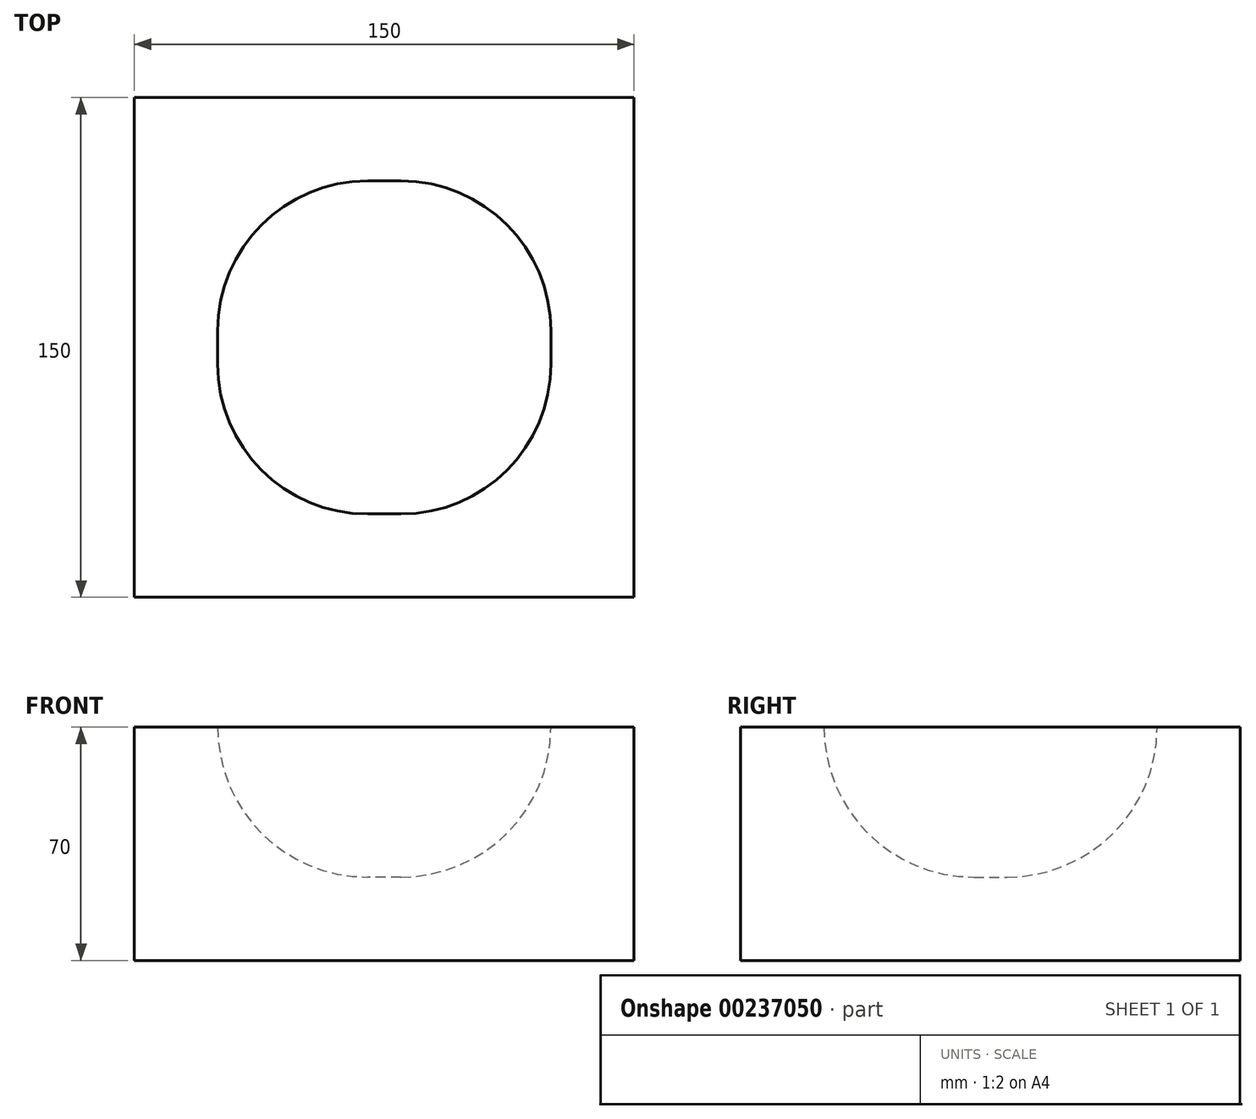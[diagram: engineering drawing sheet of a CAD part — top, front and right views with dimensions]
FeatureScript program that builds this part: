
annotation { "Feature Type Name" : "Feature", "Feature Type Description" : "" }
export const myFeature = defineFeature(function(context is Context, id is Id, definition is map)
    precondition{}
    {
        {
            var Q0;
            Q0=qCreatedBy(makeId("Top.planeOp"),FACE);
            var sketch = newSketch(context, id + "F0", { "sketchPlane" : qUnion([Q0])});
            skLineSegment(sketch, "E0.bottom", {"start": v(75, -75) * mm, "end": v(-75, -75) * mm});
            skLineSegment(sketch, "E0.top", {"start": v(75, 75) * mm, "end": v(-75, 75) * mm});
            skLineSegment(sketch, "E0.left", {"start": v(75, -75) * mm, "end": v(75, 75) * mm});
            skLineSegment(sketch, "E0.right", {"start": v(-75, -75) * mm, "end": v(-75, 75) * mm});
            skPoint(sketch, "E0.middle", {"position": v(0, 0) * mm});
            skSolve(sketch);
        }
        {
            var Q0;
            Q0=makeQuery(id+"F0.imprint","IMPRINT",FACE,{"disambiguationData":[TD([[makeQuery(id+"F0.imprint","IMPRINT",EDGE,{"derivedFrom":sQuery(id+"F0.wireOp",EDGE,"E0.bottom")}),-1.0]])]});
            extrude(context, id + "F1", {"entities" : qUnion([Q0]), "depth" : 70 * mm});
        }
        {
            var Q0;
            Q0=makeQuery(id+"F1.opExtrude","CAP_FACE",FACE,{"disambiguationData":[OSD([sQuery(id+"F0.wireOp",EDGE,"E0.bottom"),sQuery(id+"F0.wireOp",EDGE,"E0.top"),sQuery(id+"F0.wireOp",EDGE,"E0.left"),sQuery(id+"F0.wireOp",EDGE,"E0.right")])],"isStart":false});
            shell(context, id + "F2", {"entities" : qUnion([Q0]), "thickness" : 25 * mm});
        }
        {
            var Q0;
            {var subQ0=sQuery(id+"F0.wireOp",EDGE,"E0.top");Q0=makeQuery(id+"F2.opShell","OFFSET_EDGE",EDGE,{"disambiguationData":[OSD([subQ0]),TDD([makeQuery(id+"F1.opExtrude","CAP_EDGE",EDGE,{"disambiguationData":[OSD([subQ0])],"isStart":true})])]});}
            var Q1;
            {var subQ0=sQuery(id+"F0.wireOp",EDGE,"E0.right");Q1=makeQuery(id+"F2.opShell","OFFSET_EDGE",EDGE,{"disambiguationData":[OSD([subQ0]),TDD([makeQuery(id+"F1.opExtrude","CAP_EDGE",EDGE,{"disambiguationData":[OSD([subQ0])],"isStart":true})])]});}
            var Q2;
            {var subQ0=sQuery(id+"F0.wireOp",EDGE,"E0.left");Q2=makeQuery(id+"F2.opShell","OFFSET_EDGE",EDGE,{"disambiguationData":[OSD([subQ0]),TDD([makeQuery(id+"F1.opExtrude","CAP_EDGE",EDGE,{"disambiguationData":[OSD([subQ0])],"isStart":true})])]});}
            var Q3;
            {var subQ0=sQuery(id+"F0.wireOp",EDGE,"E0.bottom");Q3=makeQuery(id+"F2.opShell","OFFSET_EDGE",EDGE,{"disambiguationData":[OSD([subQ0]),TDD([makeQuery(id+"F1.opExtrude","CAP_EDGE",EDGE,{"disambiguationData":[OSD([subQ0])],"isStart":true})])]});}
            var Q4;
            Q4=makeQuery(id+"F2.opShell","OFFSET_EDGE",EDGE,{"disambiguationData":[OSD([sQuery(id+"F0.wireOp",EDGE,"E0.bottom"),sQuery(id+"F0.wireOp",EDGE,"E0.left")])]});
            var Q5;
            Q5=makeQuery(id+"F2.opShell","OFFSET_EDGE",EDGE,{"disambiguationData":[OSD([sQuery(id+"F0.wireOp",EDGE,"E0.top"),sQuery(id+"F0.wireOp",EDGE,"E0.left")])]});
            var Q6;
            Q6=makeQuery(id+"F2.opShell","OFFSET_EDGE",EDGE,{"disambiguationData":[OSD([sQuery(id+"F0.wireOp",EDGE,"E0.top"),sQuery(id+"F0.wireOp",EDGE,"E0.right")])]});
            var Q7;
            Q7=makeQuery(id+"F2.opShell","OFFSET_EDGE",EDGE,{"disambiguationData":[OSD([sQuery(id+"F0.wireOp",EDGE,"E0.bottom"),sQuery(id+"F0.wireOp",EDGE,"E0.right")])]});
            fillet(context, id + "F3", {"entities" : qUnion([Q0, Q1, Q2, Q3, Q4, Q5, Q6, Q7]), "radius" : 45 * mm, "tangentPropagation" : true, "allowEdgeOverflow" : false});
        }
    });
